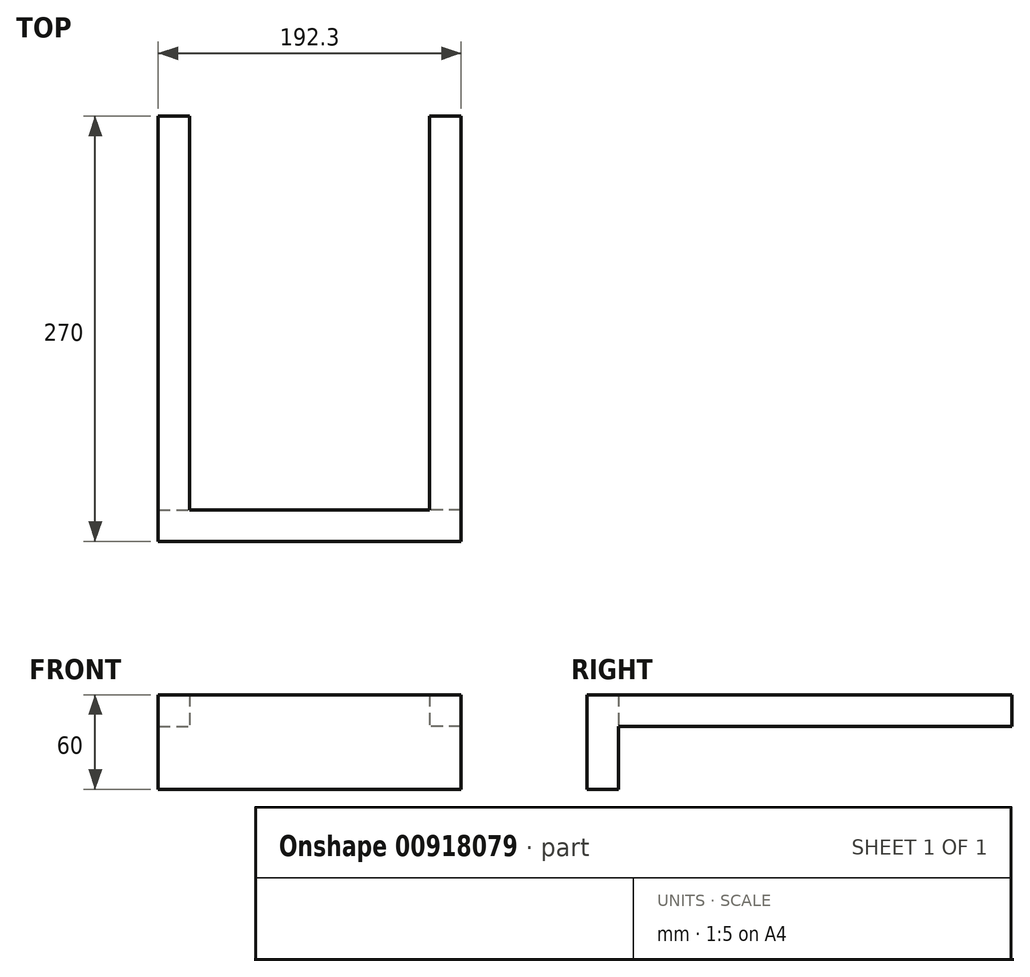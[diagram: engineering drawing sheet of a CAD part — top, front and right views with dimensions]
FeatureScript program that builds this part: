
annotation { "Feature Type Name" : "Feature", "Feature Type Description" : "" }
export const myFeature = defineFeature(function(context is Context, id is Id, definition is map)
    precondition{}
    {
        {
            var Q0;
            Q0=qCreatedBy(makeId("Front.planeOp"),FACE);
            var sketch = newSketch(context, id + "F0", { "sketchPlane" : qUnion([Q0])});
            skLineSegment(sketch, "E0.rect.bottom", {"start": v(96.15, -30) * mm, "end": v(-96.15, -30) * mm});
            skLineSegment(sketch, "E0.rect.top", {"start": v(96.15, 30) * mm, "end": v(-96.15, 30) * mm});
            skLineSegment(sketch, "E0.rect.left", {"start": v(96.15, -30) * mm, "end": v(96.15, 30) * mm});
            skLineSegment(sketch, "E0.rect.right", {"start": v(-96.15, -30) * mm, "end": v(-96.15, 30) * mm});
            skPoint(sketch, "E0.rect.middle", {"position": v(0, 0) * mm});
            skSolve(sketch);
        }
        {
            var Q0;
            Q0=qSketchRegion(id+"F0",true);
            extrude(context, id + "F1", {"entities" : qUnion([Q0]), "depth" : 20 * mm});
        }
        {
            var Q0;
            Q0=makeQuery(id+"F1.opExtrude","CAP_FACE",FACE,{"disambiguationData":[OSD([sQuery(id+"F0.wireOp",EDGE,"E0.rect.bottom"),sQuery(id+"F0.wireOp",EDGE,"E0.rect.top"),sQuery(id+"F0.wireOp",EDGE,"E0.rect.left"),sQuery(id+"F0.wireOp",EDGE,"E0.rect.right")])],"isStart":true});
            var sketch = newSketch(context, id + "F2", { "sketchPlane" : qUnion([Q0])});
            skLineSegment(sketch, "E1.bottom", {"start": v(-96.15, 30) * mm, "end": v(-76.15, 30) * mm});
            skLineSegment(sketch, "E1.top", {"start": v(-96.15, 10) * mm, "end": v(-76.15, 10) * mm});
            skLineSegment(sketch, "E1.left", {"start": v(-96.15, 30) * mm, "end": v(-96.15, 10) * mm});
            skLineSegment(sketch, "E1.right", {"start": v(-76.15, 30) * mm, "end": v(-76.15, 10) * mm});
            skLineSegment(sketch, "E2.bottom", {"start": v(96.15, 30) * mm, "end": v(76.15, 30) * mm});
            skLineSegment(sketch, "E2.top", {"start": v(96.15, 10) * mm, "end": v(76.15, 10) * mm});
            skLineSegment(sketch, "E2.left", {"start": v(96.15, 30) * mm, "end": v(96.15, 10) * mm});
            skLineSegment(sketch, "E2.right", {"start": v(76.15, 30) * mm, "end": v(76.15, 10) * mm});
            skSolve(sketch);
        }
        {
            var Q0;
            Q0=qSketchRegion(id+"F2",true);
            extrude(context, id + "F3", {"entities" : qUnion([Q0]), "operationType" : NewBodyOperationType.ADD, "depth" : 250 * mm});
        }
    });
